# Revit family: 1LA-MARZOCCO_MODBAR_POUR_OVER
name_source: partatom
category: Specialty Equipment
revit_build: Autodesk Revit 2017 (Build: 20160225_1515(x64)
units: mm (PartAtom-declared; Revit-internal decimal feet)

## family parameters
Cut with Voids When Loaded = No
Host = Face
Part Type = Normal
Room Calculation Point = Yes
Round Connector Dimension = Use Diameter
Shared = No

## types (2) — shared parameters
AMPERAGE = 20 A
BIM BADGE = https://bim.archiproducts.com
COLD WATER FLOW = 8.0 L/min
COLD WATER PRESSURE = Min 3 bar / Max 5 bar
COLD WATER SIZE = 3/8"
CUT HOLE DIMENSION = 190x260 mm (max 195x270 mm) - Tap: Ø38.1 mm (max Ø42 mm)
CUT HOLE TEMPLATE = https://modbar.com
DRAIN CONNECTION = Drain connection is 3/4" female pushfit.
Default Elevation = 1219 mm
Description = Brewer
ELECTRICIAN SPECIFICATIONS = All modules will be supplied with a NEMA 6-20P plug end on the power cord. Receptacle should be no further than 5 feet from the modules, with the electrician responsible for installation of NEMA 6-20R.
FOODSERVICE EQUIPMENT IDENTIFIER = Yes
IDENTIFY QUANTITY AS LOT = Yes
INDIRECT WASTE SIZE = 3/4"
MODULE DEPTH = 356 mm
MODULE HEIGHT = 137 mm
MODULE WIDTH = 406 mm
Manufacturer = LA MARZOCCO
Model = Modbar Pour Over
NUMBER OF POLES = 1
PHASE = 1
PRODUCT SHEET = https://www.archiproducts.com
REQUIRED MODULE CLEARANCE = Min W559 x D508 x H290 mm
TAP HEIGHT = 454 mm
TECHNICAL SHEET = https://modbar.com
URL = https://it.lamarzocco.com
WASTE OUTLET = Open gravity drain of minimum 1 1/2'' interior diameter within 4 feet of module(s). Drain must be located lower than the placement of the bottom-most module in your Modbar system. There should be no less than 1'' per foot downward slope in drain line.
WATTAGE = 3000 W

## per-type parameters (varying)
| type | TAP DEPTH | TAP WIDTH | VOLTAGE |
| MODBAR_POUR_OVER_220V | 152 mm | 178 mm | 220 V |
| MODBAR_POUR_OVER_240V | 235 mm | 175 mm | 240 V |

## geometry (parser evidence)
native form markers: Sweep x7
no freeform markers — native parametric forms only
